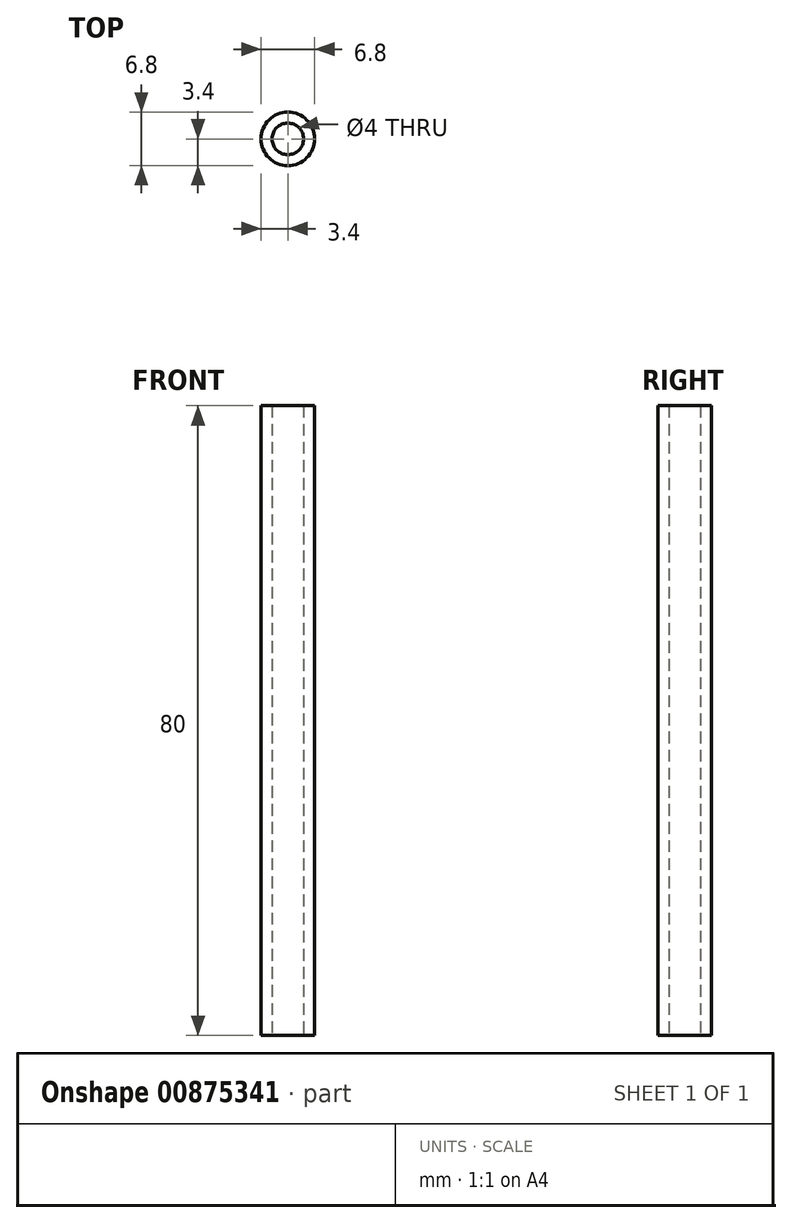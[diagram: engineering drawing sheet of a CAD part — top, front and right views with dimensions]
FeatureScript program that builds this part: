
annotation { "Feature Type Name" : "Feature", "Feature Type Description" : "" }
export const myFeature = defineFeature(function(context is Context, id is Id, definition is map)
    precondition{}
    {
        {
            var Q0;
            Q0=qCreatedBy(makeId("Top.planeOp"),FACE);
            var sketch = newSketch(context, id + "F0", { "sketchPlane" : qUnion([Q0])});
            skCircle(sketch, "E0", {"center": v(0, 0) * mm, "radius": 3.4 * mm});
            skCircle(sketch, "E1", {"center": v(0, 0) * mm, "radius": 2 * mm});
            skSolve(sketch);
        }
        {
            var Q0;
            Q0=makeQuery(id+"F0.imprint","IMPRINT",FACE,{"disambiguationData":[TD([[makeQuery(id+"F0.imprint","IMPRINT",EDGE,{"derivedFrom":sQuery(id+"F0.wireOp",EDGE,"E0")}),1.0]])]});
            extrude(context, id + "F1", {"entities" : qUnion([Q0]), "depth" : 80 * mm, "offsetDistance" : 25.4 * mm});
        }
    });
